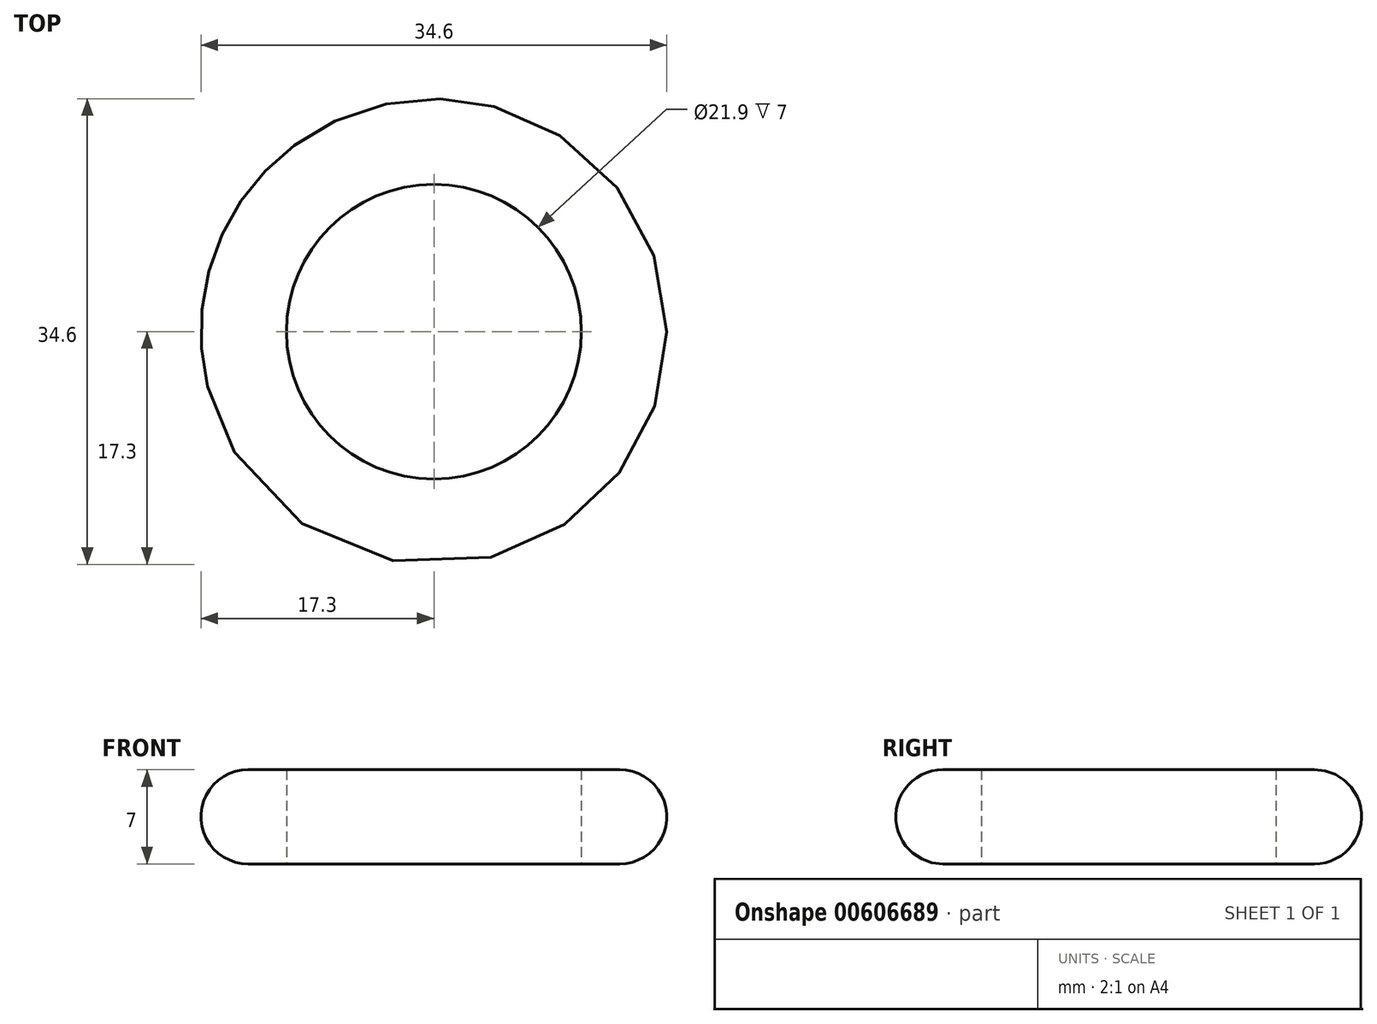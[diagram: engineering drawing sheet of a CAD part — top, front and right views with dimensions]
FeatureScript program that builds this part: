
annotation { "Feature Type Name" : "Feature", "Feature Type Description" : "" }
export const myFeature = defineFeature(function(context is Context, id is Id, definition is map)
    precondition{}
    {
        {
            var Q0;
            Q0=qCreatedBy(makeId("Top.planeOp"),FACE);
            var sketch = newSketch(context, id + "F0", { "sketchPlane" : qUnion([Q0])});
            skCircle(sketch, "E0", {"center": v(0, 0) * mm, "radius": 10.95 * mm});
            skCircle(sketch, "E1", {"center": v(0, 0) * mm, "radius": 17.3 * mm});
            skSolve(sketch);
        }
        {
            var Q0;
            Q0=makeQuery(id+"F0.imprint","IMPRINT",FACE,{"disambiguationData":[TD([[makeQuery(id+"F0.imprint","IMPRINT",EDGE,{"derivedFrom":sQuery(id+"F0.wireOp",EDGE,"E0")}),-1.0]])]});
            extrude(context, id + "F1", {"entities" : qUnion([Q0]), "depth" : 3.5 * mm, "offsetDistance" : 25.4 * mm});
        }
        {
            var Q0;
            Q0=makeQuery(id+"F1.opExtrude","CAP_FACE",FACE,{"disambiguationData":[OSD([sQuery(id+"F0.wireOp",EDGE,"E0"),sQuery(id+"F0.wireOp",EDGE,"E1")])],"isStart":true});
            extrude(context, id + "F2", {"entities" : qUnion([Q0]), "operationType" : NewBodyOperationType.ADD, "depth" : 3.5 * mm, "offsetDistance" : 25.4 * mm});
        }
        {
            var Q0;
            Q0=makeQuery(id+"F1.opExtrude","CAP_EDGE",EDGE,{"disambiguationData":[OSD([sQuery(id+"F0.wireOp",EDGE,"E1")])],"isStart":false});
            fillet(context, id + "F3", {"entities" : qUnion([Q0]), "radius" : 3.5 * mm, "tangentPropagation" : true, "allowEdgeOverflow" : false});
        }
        {
            var Q0;
            Q0=makeQuery(id+"F2.opExtrude","CAP_EDGE",EDGE,{"disambiguationData":[OSD([sQuery(id+"F0.wireOp",EDGE,"E1")])],"isStart":false});
            fillet(context, id + "F4", {"entities" : qUnion([Q0]), "radius" : 3.5 * mm, "tangentPropagation" : true, "allowEdgeOverflow" : false});
        }
    });
